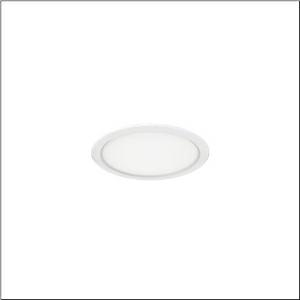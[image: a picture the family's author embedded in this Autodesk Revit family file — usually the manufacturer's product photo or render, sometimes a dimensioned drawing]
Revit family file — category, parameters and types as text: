
# Revit family: lunis_41_eco_51ds107d33b
name_source: partatom
category: Lighting Fixtures
units: mm (PartAtom-declared; Revit-internal decimal feet)

## family parameters
Cut with Voids When Loaded = No
Host = Face
Light Source = No
Part Type = Normal
Room Calculation Point = No
Round Connector Dimension = Use Diameter
Shared = No

## types (1)
- Lunis 41 Eco (1 x LED, 1460 lm, 12 W, 3000K)
    Apparent Load = 12 VA
    CIE Flux Codes = 47 80 97 100 100
    Color Rendering = 80
    Color Temperature = 3000K
    Default Elevation = 1800 mm
    Description = Lunis 41,  Eco, downlight, light emission: direct distribution, LED rated luminous flux: 1.460lm, light colour: 830, mains connection: 230V, AC, 50/60Hz, housing, round, of aluminium, coated, traffic white (RAL 9016), diameter: 166mm, recess depth: 54mm, protection rating (complete): IP20, protection rating (on room side): IP40, insulation class (complete): insulation class II (safety insulation), certification: CE, permissible ambient temperature for indoor applications: -20..+40°C, packaging unit: 1 piece
    Height = 0 mm  [stored 0 ft]
    Lamp = 1 x LED
    Lamp Light Flux = 1460 lm
    Lamp Power = 12 W
    Lamp count = 1
    Length = 166 mm
    Luminous efficacy = 122 lm/W
    Manufacturer = Siteco
    ModVariant = No
    Model = 51DS107D33B
    Mounting Place = Ceiling
    Mounting Type = Recessed
    Number of Poles = 1
    OnlyDefault = Yes
    Power Factor = 1
    Product Name = Lunis 41 Eco
    Product group = downlight
    ProductGroupID = 400
    Protection Class = Protection class II
    Protection Degree = IP 20
    RLX_Detail_Level = 1
    RLX_Emergency_Light_Flux = 0 lm
    RLX_Emergency_Type = 0
    RLX_Emergency_Type_DB = No
    RlxData = <blob elided: 8901 chars, md5=6ad42f65>
    Socket = socket
    Standby Power = 0 W
    System Light Flux = 1460 lm
    System Power = 12 W
    Type Comments = Product without accessories
    Type Image = l_1345912.jpg
    URL = http://relux.com
    VarID = ---
    Voltage = 0 V
    Weight = 0.00 kg
    Width = 0 mm  [stored 0 ft]

note: [stored X ft] marks values corroborated as IEEE doubles in the binary element streams (Revit-internal decimal feet)

## geometry (parser evidence)
native form markers: Sweep x7
no freeform markers — native parametric forms only
